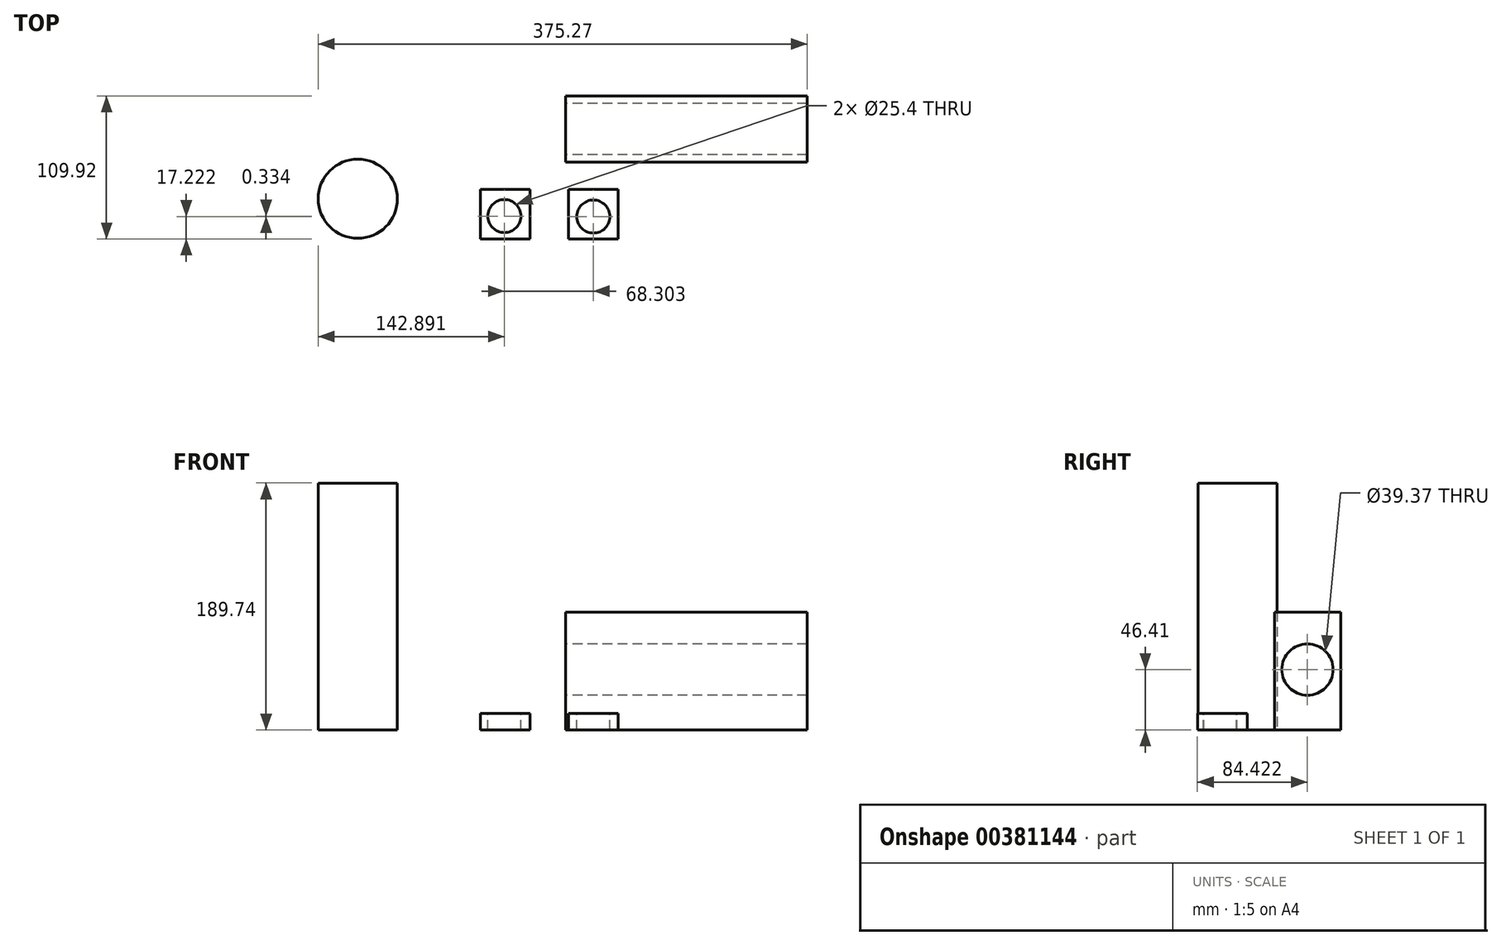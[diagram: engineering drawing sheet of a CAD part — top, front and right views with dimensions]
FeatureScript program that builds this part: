
annotation { "Feature Type Name" : "Feature", "Feature Type Description" : "" }
export const myFeature = defineFeature(function(context is Context, id is Id, definition is map)
    precondition{}
    {
        {
            var Q0;
            Q0=qCreatedBy(makeId("Top.planeOp"),FACE);
            var sketch = newSketch(context, id + "F0", { "sketchPlane" : qUnion([Q0])});
            skCircle(sketch, "E0", {"center": v(-146.98, 7.1) * mm, "radius": 30.4 * mm});
            skLineSegment(sketch, "E1.bottom", {"start": v(12.64, 86.15) * mm, "end": v(197.89, 86.15) * mm});
            skLineSegment(sketch, "E1.top", {"start": v(12.64, 35.35) * mm, "end": v(197.89, 35.35) * mm});
            skLineSegment(sketch, "E1.left", {"start": v(12.64, 86.15) * mm, "end": v(12.64, 35.35) * mm});
            skLineSegment(sketch, "E1.right", {"start": v(197.89, 86.15) * mm, "end": v(197.89, 35.35) * mm});
            skSolve(sketch);
        }
        {
            var Q0;
            Q0=makeQuery(id+"F0.imprint","IMPRINT",FACE,{"disambiguationData":[TD([[makeQuery(id+"F0.imprint","IMPRINT",EDGE,{"derivedFrom":sQuery(id+"F0.wireOp",EDGE,"E0")}),1.0]])]});
            var Q1;
            Q1=makeQuery(id+"F0.imprint","IMPRINT",FACE,{"disambiguationData":[TD([[makeQuery(id+"F0.imprint","IMPRINT",EDGE,{"derivedFrom":sQuery(id+"F0.wireOp",EDGE,"E1.bottom")}),-1.0]])]});
            extrude(context, id + "F1", {"entities" : qUnion([Q0, Q1]), "depth" : 90.68 * mm});
        }
        {
            var Q0;
            Q0=makeQuery(id+"F1.opExtrude","SWEPT_FACE",FACE,{"disambiguationData":[OSD([sQuery(id+"F0.wireOp",EDGE,"E1.left")])]});
            var sketch = newSketch(context, id + "F2", { "sketchPlane" : qUnion([Q0])});
            skCircle(sketch, "E2", {"center": v(-60.65, 46.4) * mm, "radius": 19.69 * mm});
            skSolve(sketch);
        }
        {
            var Q0;
            Q0=makeQuery(id+"F2.imprint","IMPRINT",FACE,{"disambiguationData":[TD([[makeQuery(id+"F2.imprint","IMPRINT",EDGE,{"derivedFrom":sQuery(id+"F2.wireOp",EDGE,"E2")}),1.0]])]});
            extrude(context, id + "F3", {"entities" : qUnion([Q0]), "operationType" : NewBodyOperationType.REMOVE, "oppositeDirection" : true, "depth" : 254 * mm});
        }
        {
            var Q0;
            Q0=makeQuery(id+"F1.opExtrude","CAP_FACE",FACE,{"disambiguationData":[OSD([sQuery(id+"F0.wireOp",EDGE,"E0")])],"isStart":false});
            extrude(context, id + "F4", {"entities" : qUnion([Q0]), "operationType" : NewBodyOperationType.ADD, "depth" : 72.64 * mm});
        }
        {
            var Q0;
            Q0=makeQuery(id+"F4.opExtrude","CAP_FACE",FACE,{"disambiguationData":[OSD([sQuery(id+"F0.wireOp",EDGE,"E0")])],"isStart":false});
            extrude(context, id + "F5", {"entities" : qUnion([Q0]), "operationType" : NewBodyOperationType.REMOVE, "oppositeDirection" : true, "depth" : 163.45 * mm});
        }
        {
            var Q0;
            Q0=makeQuery(id+"F0.imprint","IMPRINT",FACE,{"disambiguationData":[TD([[makeQuery(id+"F0.imprint","IMPRINT",EDGE,{"derivedFrom":sQuery(id+"F0.wireOp",EDGE,"E0")}),1.0]])]});
            extrude(context, id + "F6", {"entities" : qUnion([Q0]), "depth" : 189.74 * mm});
        }
        {
            var Q0;
            Q0=qCreatedBy(makeId("Top.planeOp"),FACE);
            var sketch = newSketch(context, id + "F7", { "sketchPlane" : qUnion([Q0])});
            skLineSegment(sketch, "E3.bottom", {"start": v(-52.86, 14.33) * mm, "end": v(-14.76, 14.33) * mm});
            skLineSegment(sketch, "E3.top", {"start": v(-52.86, -23.77) * mm, "end": v(-14.76, -23.77) * mm});
            skLineSegment(sketch, "E3.left", {"start": v(-52.86, 14.33) * mm, "end": v(-52.86, -23.77) * mm});
            skLineSegment(sketch, "E3.right", {"start": v(-14.76, 14.33) * mm, "end": v(-14.76, -23.77) * mm});
            skLineSegment(sketch, "E4", {"start": v(0, 29.52) * mm, "end": v(0, -36.6) * mm, "construction": true});
            skLineSegment(sketch, "E5.MirrorCS", {"start": v(52.86, -23.77) * mm, "end": v(14.76, -23.77) * mm});
            skLineSegment(sketch, "E6.MirrorCS", {"start": v(52.86, 14.33) * mm, "end": v(52.86, -23.77) * mm});
            skLineSegment(sketch, "E7.MirrorCS", {"start": v(52.86, 14.33) * mm, "end": v(14.76, 14.33) * mm});
            skLineSegment(sketch, "E8.MirrorCS", {"start": v(14.76, 14.33) * mm, "end": v(14.76, -23.77) * mm});
            skSolve(sketch);
        }
        {
            var Q0;
            Q0=makeQuery(id+"F7.imprint","IMPRINT",FACE,{"disambiguationData":[TD([[makeQuery(id+"F7.imprint","IMPRINT",EDGE,{"derivedFrom":sQuery(id+"F7.wireOp",EDGE,"E3.bottom")}),-1.0]])]});
            var Q1;
            Q1=makeQuery(id+"F7.imprint","IMPRINT",FACE,{"disambiguationData":[TD([[makeQuery(id+"F7.imprint","IMPRINT",EDGE,{"derivedFrom":sQuery(id+"F7.wireOp",EDGE,"E5.MirrorCS")}),-1.0]])]});
            extrude(context, id + "F8", {"entities" : qUnion([Q0, Q1]), "depth" : 12.7 * mm});
        }
        {
            var Q0;
            Q0=makeQuery(id+"F8.opExtrude","CAP_FACE",FACE,{"disambiguationData":[OSD([sQuery(id+"F7.wireOp",EDGE,"E3.bottom"),sQuery(id+"F7.wireOp",EDGE,"E3.top"),sQuery(id+"F7.wireOp",EDGE,"E3.left"),sQuery(id+"F7.wireOp",EDGE,"E3.right")])],"isStart":false});
            var sketch = newSketch(context, id + "F9", { "sketchPlane" : qUnion([Q0])});
            skCircle(sketch, "E9", {"center": v(-34.49, -6.21) * mm, "radius": 12.7 * mm});
            skSolve(sketch);
        }
        {
            var Q0;
            Q0=makeQuery(id+"F8.opExtrude","CAP_FACE",FACE,{"disambiguationData":[OSD([sQuery(id+"F7.wireOp",EDGE,"E5.MirrorCS"),sQuery(id+"F7.wireOp",EDGE,"E6.MirrorCS"),sQuery(id+"F7.wireOp",EDGE,"E7.MirrorCS"),sQuery(id+"F7.wireOp",EDGE,"E8.MirrorCS")])],"isStart":false});
            var sketch = newSketch(context, id + "F10", { "sketchPlane" : qUnion([Q0])});
            skCircle(sketch, "E10", {"center": v(33.81, -6.55) * mm, "radius": 12.7 * mm});
            skPoint(sketch, "E10.centerSnap0", {"position": v(33.81, 14.33) * mm});
            skSolve(sketch);
        }
        {
            var Q0;
            Q0=makeQuery(id+"F9.imprint","IMPRINT",FACE,{"disambiguationData":[TD([[makeQuery(id+"F9.imprint","IMPRINT",EDGE,{"derivedFrom":sQuery(id+"F9.wireOp",EDGE,"E9")}),1.0]])]});
            extrude(context, id + "F11", {"entities" : qUnion([Q0]), "operationType" : NewBodyOperationType.REMOVE, "oppositeDirection" : true, "depth" : 25.4 * mm});
        }
        {
            var Q0;
            Q0=makeQuery(id+"F10.imprint","IMPRINT",FACE,{"disambiguationData":[TD([[makeQuery(id+"F10.imprint","IMPRINT",EDGE,{"derivedFrom":sQuery(id+"F10.wireOp",EDGE,"E10")}),1.0]])]});
            extrude(context, id + "F12", {"entities" : qUnion([Q0]), "operationType" : NewBodyOperationType.REMOVE, "oppositeDirection" : true, "depth" : 25.4 * mm});
        }
    });
